# Revit family: VL1GW1500xxWSxM9x
name_source: partatom
category: Leuchten
units: mm (PartAtom-declared; Revit-internal decimal feet)

## family parameters
Basisbauteil = Fläche
Beim Laden mit Abzugskörper schneiden = Nein
Bemaßung runder Anschluss = Durchmesser verwenden
Gemeinsam genutzt = Nein
Lichtquelle = Ja
OmniClass-Nummer = 23.80.70.11
OmniClass-Titel = Luminaries for Internal Lighting
Raumberechnungspunkt = Nein
Teiletyp = Normal

## types (6) — shared parameters
Baugruppenkennzeichen = D5020200
Emissionsform beim Rendern sichtbar = Nein
Farbfilter = 16777215
Farbtemperaturverschiebung bei Dämpfen der Lampe = <Keine Auswahl>
Hersteller = RIDI Leuchten GmbH
Lampe = LED
Neigungswinkel = 90.00°
URL = www.ridi.de
Von Breite des Rechtecks ausssenden = 1440 mm  [stored 4.72441 ft]
Von Länge des Rechtecks aussenden = 92 mm  [stored 0.301837 ft]
brand = RIDI
conformity mark = CE
electrical safety class = 1
height = 90 mm  [stored 0.295276 ft]
ingress protection (IP) code = IP20
length = 1500 mm  [stored 4.92126 ft]
nominal frequency = 50-60Hz
nominal voltage = 230
voltage type (AC, DC, UC) = AC
weight = 3,23kg
width = 95 mm
zero-valued in all types: Vorgabe-Ansicht

## per-type parameters (varying)
| type | Datei für fotometrisches Netz | Modell | Scheinlast | rated input power |
| VL1GW1500RFWS840M9S0700 | xxxM9Sxxx.IES | 1522579 | 50 VA | 50 |
| VL1GW1500DAWS840M9S0700 | xxxM9Sxxx.IES | 1532579 | 50 VA | 50 |
| VL1GW1500RFWS840M9P0800 | xxxM9Pxxx.IES | 1522580 | 50 VA | 50 |
| VL1GW1500DAWS840M9P0800 | xxxM9Pxxx.IES | 1532580 | 50 VA | 50 |
| VL1GW1500RFWS940M9P0700 | xxxM9Pxxx.IES | 1522581 | 49 VA | 49 |
| VL1GW1500DAWS940M9P0700 | xxxM9Pxxx.IES | 1532581 | 49 VA | 49 |

note: column(s) folded — value = type name in every type: product name

note: [stored X ft] marks values corroborated as IEEE doubles in the binary element streams (Revit-internal decimal feet)
